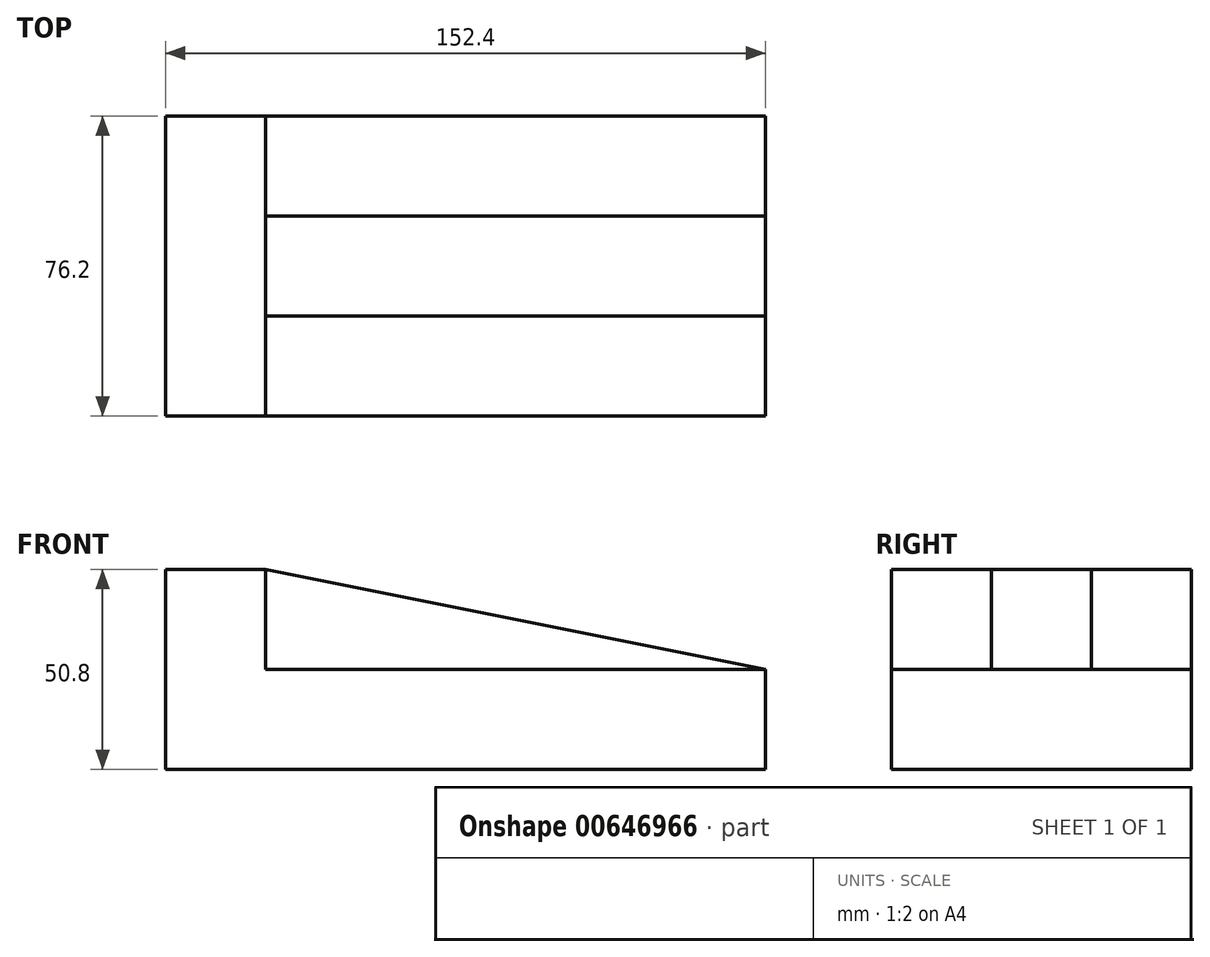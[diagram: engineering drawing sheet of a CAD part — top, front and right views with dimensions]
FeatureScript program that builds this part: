
annotation { "Feature Type Name" : "Feature", "Feature Type Description" : "" }
export const myFeature = defineFeature(function(context is Context, id is Id, definition is map)
    precondition{}
    {
        {
            var Q0;
            Q0=qCreatedBy(makeId("Front.planeOp"),FACE);
            var sketch = newSketch(context, id + "F0", { "sketchPlane" : qUnion([Q0])});
            skLineSegment(sketch, "E0.bottom", {"start": v(-85.7, 53.7) * mm, "end": v(41.3, 53.7) * mm});
            skLineSegment(sketch, "E0.top", {"start": v(-111.1, 28.3) * mm, "end": v(41.3, 28.3) * mm});
            skLineSegment(sketch, "E0.right", {"start": v(41.3, 53.7) * mm, "end": v(41.3, 28.3) * mm});
            skLineSegment(sketch, "E1.bottom", {"start": v(-111.1, 79.1) * mm, "end": v(-85.7, 79.1) * mm});
            skLineSegment(sketch, "E1.right", {"start": v(-85.7, 79.1) * mm, "end": v(-85.7, 53.7) * mm});
            skLineSegment(sketch, "E2", {"start": v(-111.1, 79.1) * mm, "end": v(-111.1, 28.3) * mm});
            skLineSegment(sketch, "E3", {"start": v(-85.7, 79.1) * mm, "end": v(41.3, 53.7) * mm});
            skSolve(sketch);
        }
        {
            var Q0;
            Q0=makeQuery(id+"F0.imprint","IMPRINT",FACE,{"disambiguationData":[TD([[makeQuery(id+"F0.imprint","IMPRINT",EDGE,{"derivedFrom":sQuery(id+"F0.wireOp",EDGE,"E0.bottom")}),-1.0]])]});
            extrude(context, id + "F1", {"entities" : qUnion([Q0]), "oppositeDirection" : true, "depth" : 50.8 * mm, "offsetDistance" : 25.4 * mm});
        }
        {
            var Q0;
            Q0=makeQuery(id+"F0.imprint","IMPRINT",FACE,{"disambiguationData":[TD([[makeQuery(id+"F0.imprint","IMPRINT",EDGE,{"derivedFrom":sQuery(id+"F0.wireOp",EDGE,"E0.bottom")}),-1.0]])]});
            extrude(context, id + "F2", {"entities" : qUnion([Q0]), "operationType" : NewBodyOperationType.ADD, "depth" : 25.4 * mm, "offsetDistance" : 25.4 * mm});
        }
        {
            var Q0;
            Q0=makeQuery(id+"F0.imprint","IMPRINT",FACE,{"disambiguationData":[TD([[makeQuery(id+"F0.imprint","IMPRINT",EDGE,{"derivedFrom":sQuery(id+"F0.wireOp",EDGE,"E0.bottom")}),1.0]])]});
            extrude(context, id + "F3", {"entities" : qUnion([Q0]), "operationType" : NewBodyOperationType.ADD, "oppositeDirection" : true, "depth" : 25.4 * mm, "offsetDistance" : 25.4 * mm});
        }
    });
